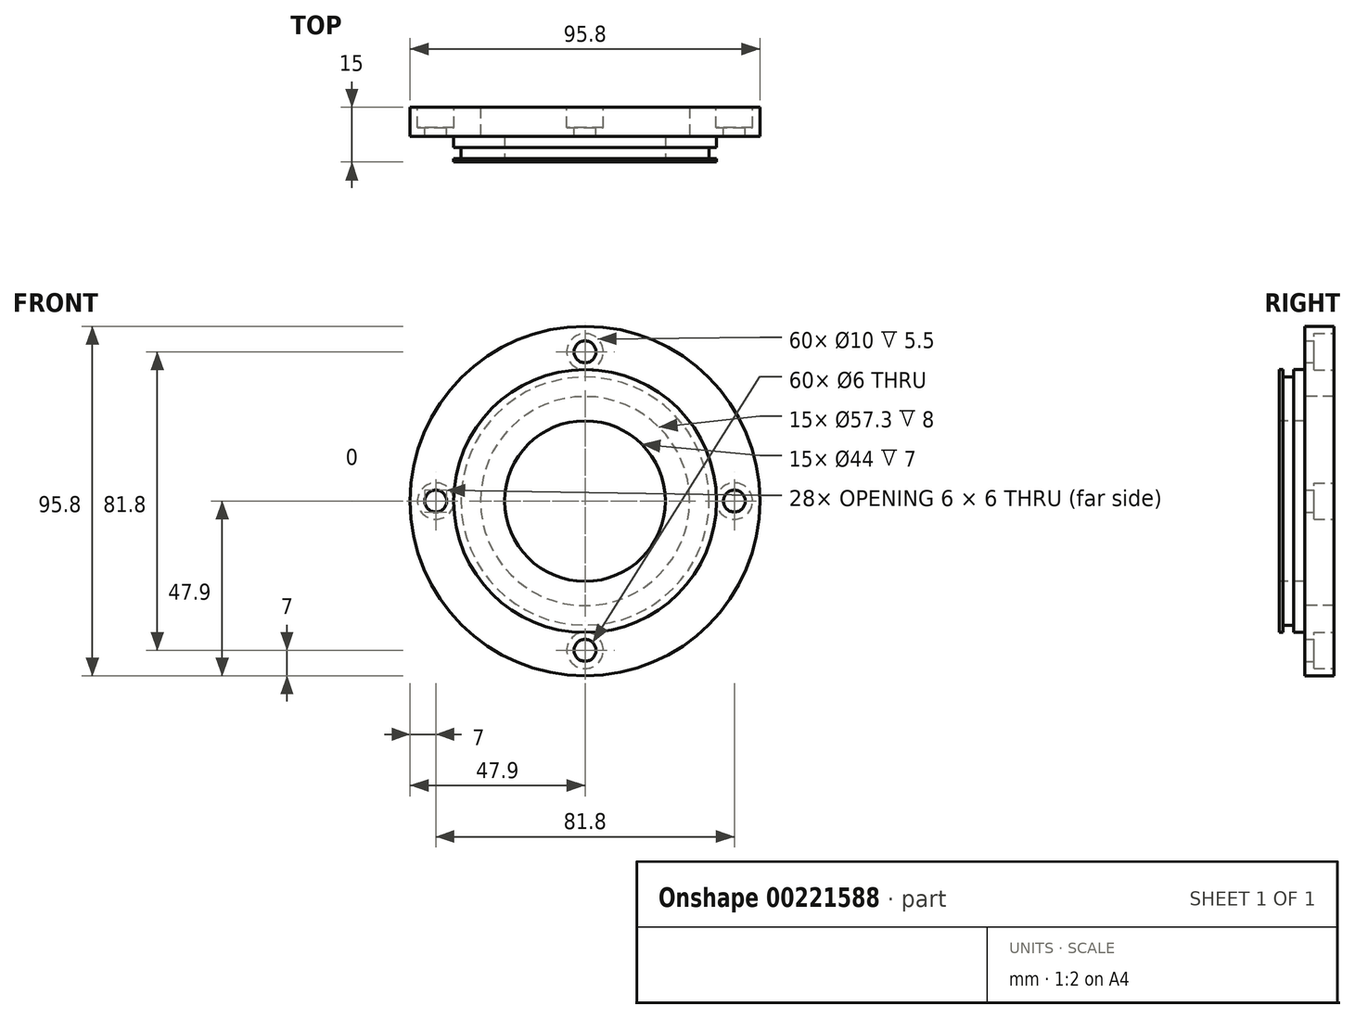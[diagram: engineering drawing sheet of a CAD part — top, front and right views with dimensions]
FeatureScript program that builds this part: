
annotation { "Feature Type Name" : "Feature", "Feature Type Description" : "" }
export const myFeature = defineFeature(function(context is Context, id is Id, definition is map)
    precondition{}
    {
        {
            var Q0;
            Q0=qCreatedBy(makeId("Right.planeOp"),FACE);
            var sketch = newSketch(context, id + "F0", { "sketchPlane" : qUnion([Q0])});
            skLineSegment(sketch, "E0", {"start": v(-112.13, 0) * mm, "end": v(113.78, 0) * mm, "construction": true});
            skLineSegment(sketch, "E1", {"start": v(0, 0) * mm, "end": v(0, 28.65) * mm, "construction": true});
            skLineSegment(sketch, "E2", {"start": v(0, 28.65) * mm, "end": v(0, 47.9) * mm});
            skLineSegment(sketch, "E3", {"start": v(0, 47.9) * mm, "end": v(-8, 47.9) * mm});
            skLineSegment(sketch, "E4", {"start": v(-8, 47.9) * mm, "end": v(-8, 36) * mm});
            skLineSegment(sketch, "E5", {"start": v(-8, 36) * mm, "end": v(-11, 36) * mm});
            skLineSegment(sketch, "E6", {"start": v(-11, 36) * mm, "end": v(-11, 34) * mm});
            skLineSegment(sketch, "E7", {"start": v(-11, 34) * mm, "end": v(-14, 34) * mm});
            skLineSegment(sketch, "E8", {"start": v(-14, 34) * mm, "end": v(-14, 36) * mm});
            skLineSegment(sketch, "E9", {"start": v(-14, 36) * mm, "end": v(-15, 36) * mm});
            skLineSegment(sketch, "E10", {"start": v(-15, 36) * mm, "end": v(-15, 22) * mm});
            skLineSegment(sketch, "E11", {"start": v(-15, 22) * mm, "end": v(-15, 22) * mm});
            skLineSegment(sketch, "E12", {"start": v(-15, 22) * mm, "end": v(-15, 0) * mm, "construction": true});
            skLineSegment(sketch, "E13", {"start": v(-15, 22) * mm, "end": v(-8, 22) * mm});
            skLineSegment(sketch, "E14", {"start": v(-8, 22) * mm, "end": v(-8, 28.65) * mm});
            skLineSegment(sketch, "E15", {"start": v(-8, 28.65) * mm, "end": v(0, 28.65) * mm});
            skSolve(sketch);
        }
        {
            var Q0;
            Q0=makeQuery(id+"F0.imprint","IMPRINT",FACE,{"disambiguationData":[TD([[makeQuery(id+"F0.imprint","IMPRINT",EDGE,{"derivedFrom":sQuery(id+"F0.wireOp",EDGE,"E2")}),1.0]])]});
            var Q1;
            Q1=sQuery(id+"F0.wireOp",EDGE,"E0");
            revolve(context, id + "F1", {"entities" : qUnion([Q0]), "axis" : qUnion([Q1]), "revolveType" : RevolveType.FULL});
        }
        {
            var Q0;
            Q0=qCreatedBy(makeId("Front.planeOp"),FACE);
            var sketch = newSketch(context, id + "F2", { "sketchPlane" : qUnion([Q0])});
            skCircle(sketch, "E16", {"center": v(0, 0) * mm, "radius": 40.9 * mm, "construction": true});
            skCircle(sketch, "E17", {"center": v(0, 40.9) * mm, "radius": 5 * mm});
            skCircle(sketch, "E18", {"center": v(0, 40.9) * mm, "radius": 3 * mm});
            skCircle(sketch, "E19.1.0", {"center": v(-40.9, 0) * mm, "radius": 5 * mm});
            skCircle(sketch, "E19.1.1", {"center": v(-40.9, 0) * mm, "radius": 3 * mm});
            skCircle(sketch, "E19.2.0", {"center": v(0, -40.9) * mm, "radius": 5 * mm});
            skCircle(sketch, "E19.2.1", {"center": v(0, -40.9) * mm, "radius": 3 * mm});
            skCircle(sketch, "E19.3.0", {"center": v(40.9, 0) * mm, "radius": 5 * mm});
            skCircle(sketch, "E19.3.1", {"center": v(40.9, 0) * mm, "radius": 3 * mm});
            skSolve(sketch);
        }
        {
            var Q0;
            Q0=makeQuery(id+"F2.imprint","IMPRINT",FACE,{"disambiguationData":[TD([[makeQuery(id+"F2.imprint","IMPRINT",EDGE,{"derivedFrom":sQuery(id+"F2.wireOp",EDGE,"E17")}),1.0]])]});
            var Q1;
            Q1=makeQuery(id+"F2.imprint","IMPRINT",FACE,{"disambiguationData":[TD([[makeQuery(id+"F2.imprint","IMPRINT",EDGE,{"derivedFrom":sQuery(id+"F2.wireOp",EDGE,"E19.1.0")}),1.0]])]});
            var Q2;
            Q2=makeQuery(id+"F2.imprint","IMPRINT",FACE,{"disambiguationData":[TD([[makeQuery(id+"F2.imprint","IMPRINT",EDGE,{"derivedFrom":sQuery(id+"F2.wireOp",EDGE,"E19.3.0")}),1.0]])]});
            var Q3;
            Q3=makeQuery(id+"F2.imprint","IMPRINT",FACE,{"disambiguationData":[TD([[makeQuery(id+"F2.imprint","IMPRINT",EDGE,{"derivedFrom":sQuery(id+"F2.wireOp",EDGE,"E19.2.0")}),1.0]])]});
            var Q4;
            Q4=sQuery(id+"F2.wireOp",EDGE,"E17");
            var Q5;
            Q5=sQuery(id+"F2.wireOp",EDGE,"E18");
            var Q6;
            Q6=sQuery(id+"F2.wireOp",EDGE,"E19.3.0");
            var Q7;
            Q7=sQuery(id+"F2.wireOp",EDGE,"E19.3.1");
            var Q8;
            Q8=sQuery(id+"F2.wireOp",EDGE,"E19.1.0");
            var Q9;
            Q9=sQuery(id+"F2.wireOp",EDGE,"E19.1.1");
            var Q10;
            Q10=sQuery(id+"F2.wireOp",EDGE,"E19.2.0");
            var Q11;
            Q11=sQuery(id+"F2.wireOp",EDGE,"E19.2.1");
            extrude(context, id + "F3", {"entities" : qUnion([Q0, Q1, Q2, Q3]), "operationType" : NewBodyOperationType.REMOVE, "surfaceEntities" : qUnion([Q4, Q5, Q6, Q7, Q8, Q9, Q10, Q11]), "depth" : 5.5 * mm});
        }
        {
            var Q0;
            Q0=makeQuery(id+"F3.boolean.opBoolean","SPLIT",FACE,{"disambiguationData":[TD([makeQuery(id+"F3.opExtrude","SWEPT_FACE",FACE,{"disambiguationData":[OSD([sQuery(id+"F2.wireOp",EDGE,"E19.1.1")])]})])],"derivedFrom":makeQuery(id+"F1.opRevolve","SWEPT_FACE",FACE,{"disambiguationData":[OSD([sQuery(id+"F0.wireOp",EDGE,"E2")])]})});
            var Q1;
            Q1=makeQuery(id+"F3.boolean.opBoolean","SPLIT",FACE,{"disambiguationData":[TD([makeQuery(id+"F3.opExtrude","SWEPT_FACE",FACE,{"disambiguationData":[OSD([sQuery(id+"F2.wireOp",EDGE,"E18")])]})])],"derivedFrom":makeQuery(id+"F1.opRevolve","SWEPT_FACE",FACE,{"disambiguationData":[OSD([sQuery(id+"F0.wireOp",EDGE,"E2")])]})});
            var Q2;
            Q2=makeQuery(id+"F3.boolean.opBoolean","SPLIT",FACE,{"disambiguationData":[TD([makeQuery(id+"F3.opExtrude","SWEPT_FACE",FACE,{"disambiguationData":[OSD([sQuery(id+"F2.wireOp",EDGE,"E19.3.1")])]})])],"derivedFrom":makeQuery(id+"F1.opRevolve","SWEPT_FACE",FACE,{"disambiguationData":[OSD([sQuery(id+"F0.wireOp",EDGE,"E2")])]})});
            var Q3;
            Q3=makeQuery(id+"F3.boolean.opBoolean","SPLIT",FACE,{"disambiguationData":[TD([makeQuery(id+"F3.opExtrude","SWEPT_FACE",FACE,{"disambiguationData":[OSD([sQuery(id+"F2.wireOp",EDGE,"E19.2.1")])]})])],"derivedFrom":makeQuery(id+"F1.opRevolve","SWEPT_FACE",FACE,{"disambiguationData":[OSD([sQuery(id+"F0.wireOp",EDGE,"E2")])]})});
            extrude(context, id + "F4", {"entities" : qUnion([Q0, Q1, Q2, Q3]), "operationType" : NewBodyOperationType.REMOVE, "oppositeDirection" : true, "depth" : 25 * mm});
        }
    });
